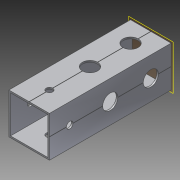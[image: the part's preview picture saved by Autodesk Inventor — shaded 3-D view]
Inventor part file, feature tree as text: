
AUTODESK INVENTOR PART (.ipt)
format: ipt  version: 2014 SP1 (Build 180222100, 222)  size: 1,226,240 bytes
history: native  units: in
note: dims shown in document units (in); Inventor stores cm internally (conversion verified against a paired STEP export)
features: extrude x3, sketch x3, pattern_circular x1, other x1, plane x1, imported_body x1
ambient origin geometry x8: Origin, YZ Plane, XZ Plane, XY Plane, X Axis, Y Axis, Z Axis, Center Point
bodies: Body1 (feature_tree)
feature tree (10):
  pattern_circular  "CirPattern2"
  other  "217-3426-STEP1"
  plane  "Work Plane1"
  extrude  "Extrusion1"  Depth=3937.0079in TaperAngle=0.0deg
  extrude  "Extrusion2"  Depth=0.375in
  extrude  "Extrusion3"  Depth=0.375in
  imported_body  "Base1"
  sketch  "Sketch1"  dims[d0=-3.0in d1=3937.0079in d2=0.0in]
  sketch  "Sketch3"  dims[d3=0.375in d4=0.375in]
  sketch  "Sketch4"  dims[d5=39.3701in d6=0.0in d7=0.375in d8=0.375in d9=39.3701in d10=0.0in]
